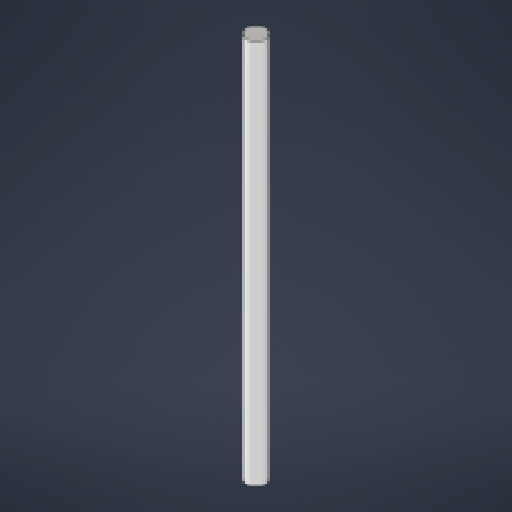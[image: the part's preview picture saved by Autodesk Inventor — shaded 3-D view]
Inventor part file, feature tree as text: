
AUTODESK INVENTOR PART (.ipt)
format: ipt  version: 2023.2 (Build 272271000, 271)  size: 118,784 bytes
history: native  units: mm
features: extrude x1, sketch x1
ambient origin geometry x8: Origin, YZ Plane, XZ Plane, XY Plane, X Axis, Y Axis, Z Axis, Center Point
bodies: Volumenkörper1 (feature_tree)
feature tree (2):
  extrude  "Extrusion1"  Depth=135.0mm TaperAngle=0.0deg
  sketch  "Skizze1"  dims[d0=6.0mm d1=135.0mm d2=0.0mm]
